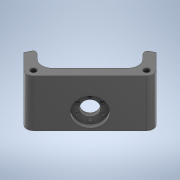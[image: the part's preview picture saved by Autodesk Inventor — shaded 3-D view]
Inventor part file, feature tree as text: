
AUTODESK INVENTOR PART (.ipt)
format: ipt  version: 2020 (Build 240168000, 168)  size: 254,464 bytes
history: native  units: mm
features: sketch x8, extrude x6, projected_geometry x4, other x1, chamfer x1
ambient origin geometry x8: Origin, YZ Plane, XZ Plane, XY Plane, X Axis, Y Axis, Z Axis, Center Point
bodies: Body1 (feature_tree)
feature tree (20):
  other  "Твердое тело1"
  extrude  "Выдавливание1"  Depth=35.0mm TaperAngle=0.0deg
  sketch  "Эскиз2"
  extrude  "Выдавливание4"  Depth=20.6mm
  extrude  "Выдавливание5"  Depth=15.0mm
  sketch  "Эскиз5"
  extrude  "Выдавливание8"  Depth=2.5mm
  extrude  "Выдавливание9"  Depth=60.0mm TaperAngle=360.0deg
  chamfer  "Фаска2"  Distance=11.0mm
  sketch  "Эскиз6"
  sketch  "Эскиз7"
  extrude  "Выдавливание11"  Depth=4.0mm
  sketch  "Эскиз1"
  projected_geometry  "Спроецированная петля1"
  sketch  "Эскиз3"
  sketch  "Эскиз4"
  projected_geometry  "Спроецированная петля2"
  sketch  "Эскиз8"
  projected_geometry  "Спроецированная петля3"
  projected_geometry  "Спроецированная петля4"
